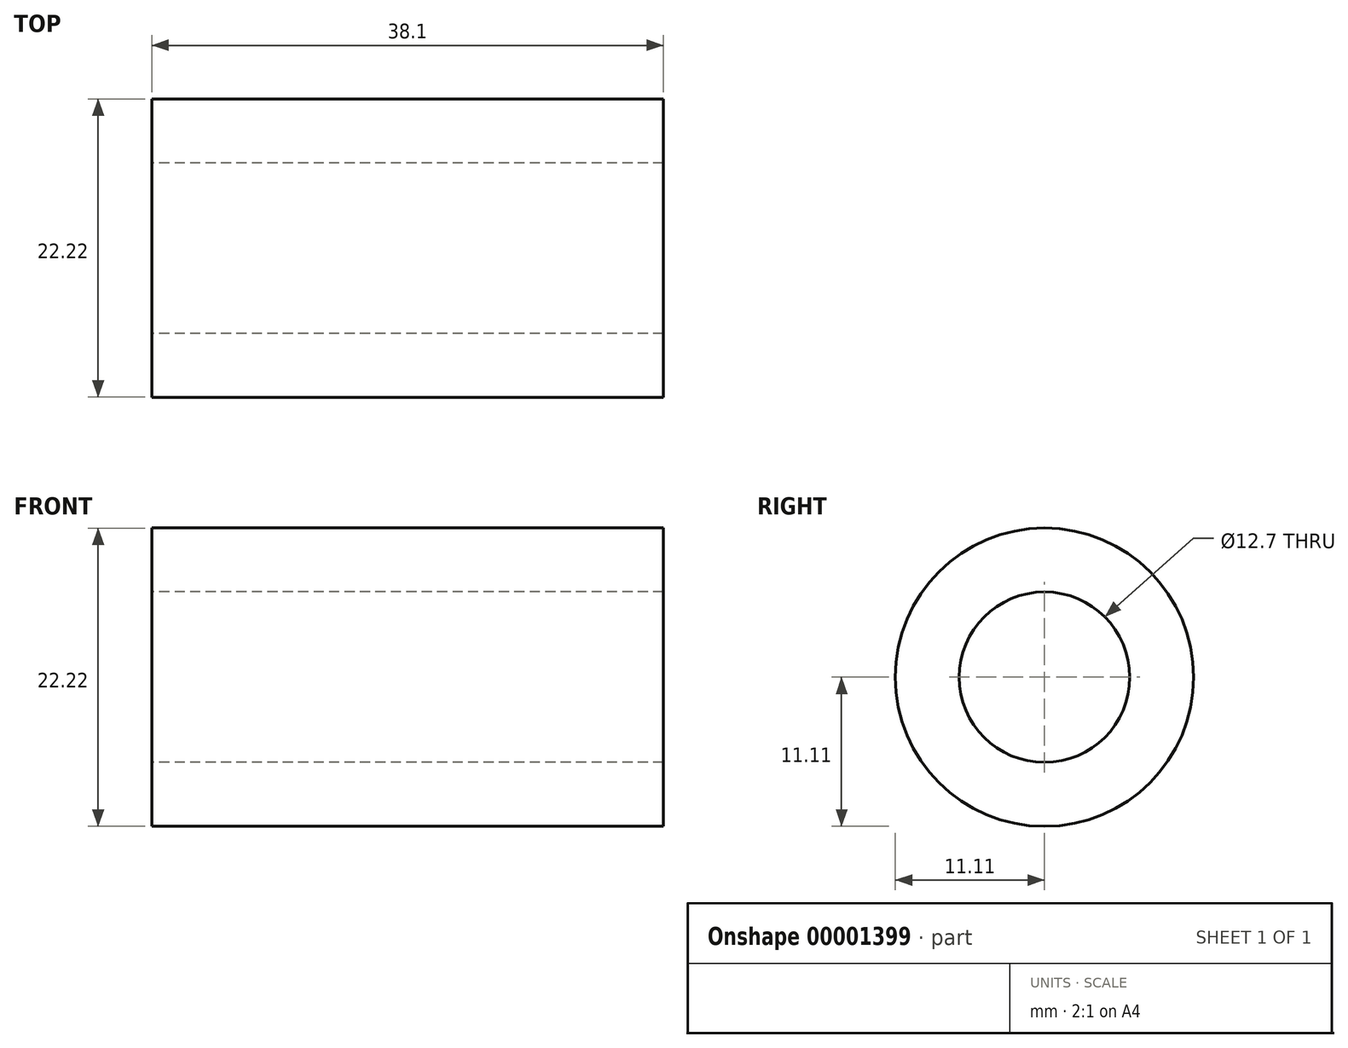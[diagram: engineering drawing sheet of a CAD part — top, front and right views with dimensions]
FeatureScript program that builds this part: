
annotation { "Feature Type Name" : "Feature", "Feature Type Description" : "" }
export const myFeature = defineFeature(function(context is Context, id is Id, definition is map)
    precondition{}
    {
        {
            var Q0;
            Q0=qCreatedBy(makeId("Right.planeOp"),FACE);
            var sketch = newSketch(context, id + "F0", { "sketchPlane" : qUnion([Q0])});
            skCircle(sketch, "E0", {"center": v(0, 0) * mm, "radius": 11.11 * mm});
            skCircle(sketch, "E1", {"center": v(0, 0) * mm, "radius": 6.35 * mm});
            skSolve(sketch);
        }
        {
            var Q0;
            Q0 = qSketchRegion(id + "F0", true);
            extrude(context, id + "F1", {"entities" : qUnion([Q0]), "endBound" : BoundingType.SYMMETRIC, "depth" : 38.1 * mm});
        }
    });
